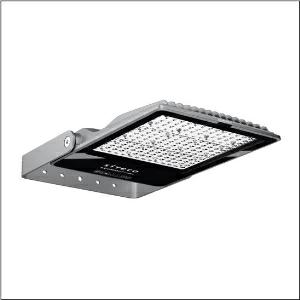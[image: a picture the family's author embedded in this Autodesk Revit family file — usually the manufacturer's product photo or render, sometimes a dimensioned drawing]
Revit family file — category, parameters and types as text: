
# Revit family: sicompact_r__31_midi___pl32_5xa7581e2k23_2195
name_source: partatom
category: Lighting Fixtures
units: mm (PartAtom-declared; Revit-internal decimal feet)

## family parameters
Cut with Voids When Loaded = No
Host = Face
Light Source = No
Part Type = Normal
Room Calculation Point = No
Round Connector Dimension = Use Diameter
Shared = No

## types (1)
- SiCompact® 31 midi  PL32 (1 x LED, 37000 lm, 243 W, 4000K)
    Apparent Load = 243 VA
    CIE Flux Codes = 32 69 98 100 100
    Color Rendering = 70
    Color Temperature = 4000K
    Default Elevation = 1800 mm
    Description = SiCompact® 31 midi, floodlight, primary light control with lens, of plastic, of toughened safety glass, transparent, light distribution: PL32, light emission: direct distribution, primary light characteristic: asymmetric, installation type: surface-mounted, LED, High Power LED, rated luminous flux: 37.000lm, luminous efficacy: 152lm/W, light colour: 740, colour temperature: 4000K, control gear: ECG, with cable, 3x 1.5mm², mains connection: 220..240V, AC, 50/60Hz, connection cable pre-assembled, cable length: 2m, rated input power: 243W, of diecast aluminium, specular, metallic grey (RAL 9006), length: 560mm, width: 330mm, height: 62mm, bracket, of sheet steel, coated, metallic grey (RAL 9006), ON/OFF, protection rating (complete): IP66, insulation class (complete): insulation class I (protective earthing), certification: CE, ENEC, impact resistance: IK08, permissible operating ambient temperature: -40..+45°C, packaging unit: 1 piece

Light Distribution: PL32
    Height = 62 mm
    Lamp = 1 x LED
    Lamp Light Flux = 37000 lm
    Lamp Power = 243 W
    Lamp count = 1
    Length = 560 mm
    Luminous efficacy = 152 lm/W
    Manufacturer = Siteco
    ModVariant = No
    Model = 5XA7581E2K23
    Mounting Place = Wall
    Mounting Type = Surface mounted
    Number of Poles = 1
    OnlyDefault = Yes
    Power Factor = 1
    Product Name = SiCompact® 31 midi | PL32
    Product group = floodlight | wall mounted
    ProductGroupID = 2001
    Protection Class = Protection class I
    Protection Degree = IP 66
    RLX_Detail_Level = 1
    RLX_Emergency_Light_Flux = 0 lm
    RLX_Emergency_Type = 0
    RLX_Emergency_Type_DB = No
    RlxData = <blob elided: 98325 chars, md5=19f95b25>
    Socket = socket
    Standby Power = 0 W
    System Light Flux = 37000 lm
    System Power = 243 W
    Type Comments = Product without accessories
    Type Image = l_1006415.jpg
    URL = http://relux.com
    VarID = ---
    Voltage = 0 V
    Weight = 0.00 kg
    Width = 333 mm

## geometry (parser evidence)
native form markers: Blend x4, Sweep x12
no freeform markers — native parametric forms only
